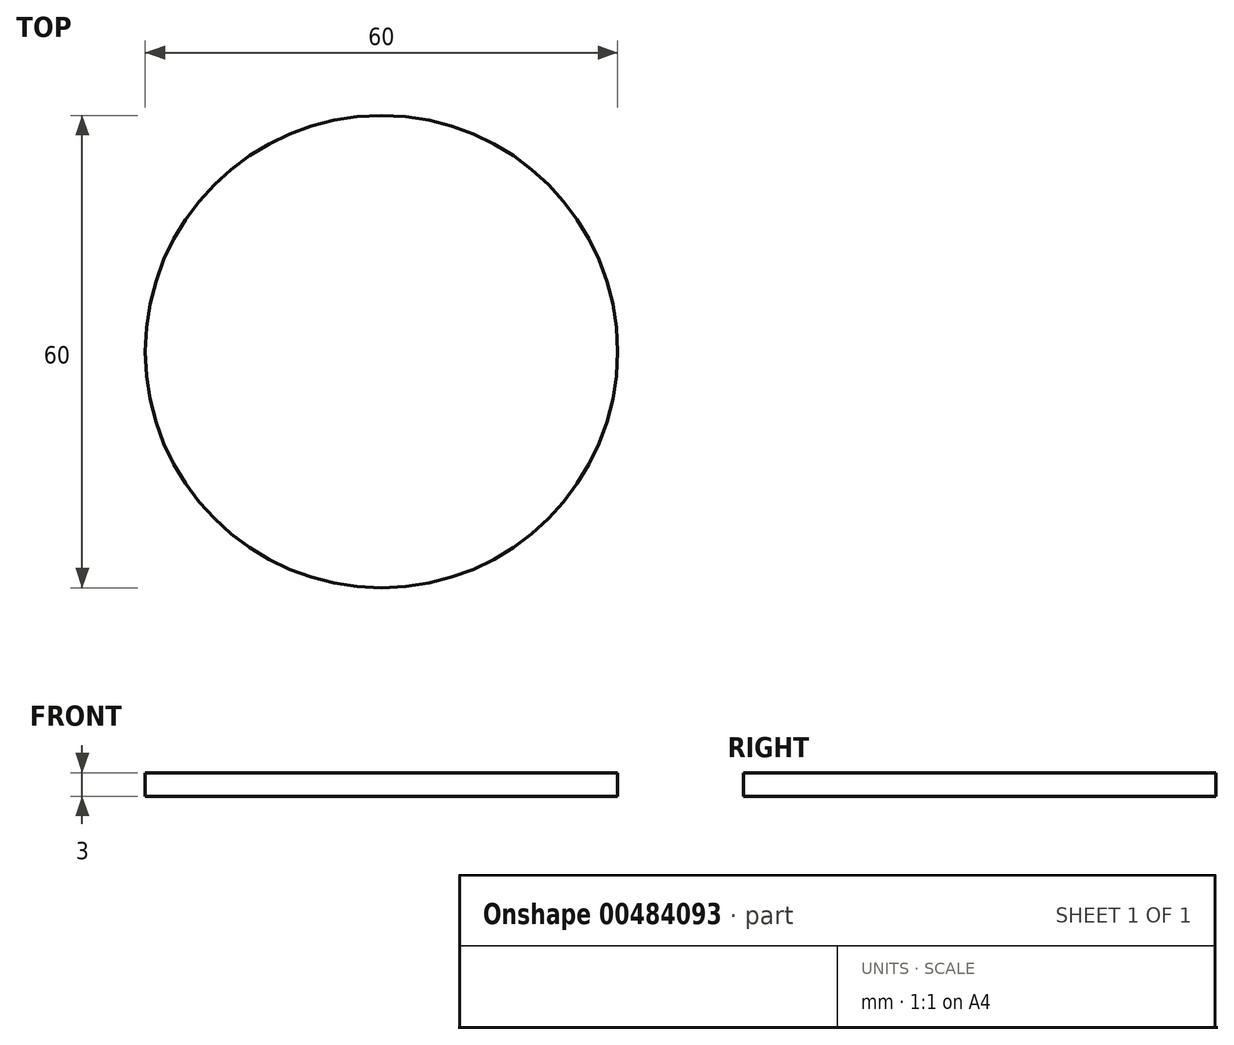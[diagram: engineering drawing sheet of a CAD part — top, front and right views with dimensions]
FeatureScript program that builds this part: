
annotation { "Feature Type Name" : "Feature", "Feature Type Description" : "" }
export const myFeature = defineFeature(function(context is Context, id is Id, definition is map)
    precondition{}
    {
        {
            var Q0;
            Q0=qCreatedBy(makeId("Top.planeOp"),FACE);
            var sketch = newSketch(context, id + "F0", { "sketchPlane" : qUnion([Q0])});
            skCircle(sketch, "E0", {"center": v(0, 0) * mm, "radius": 30 * mm});
            skSolve(sketch);
        }
        {
            var Q0;
            Q0=makeQuery(id+"F0.imprint","IMPRINT",FACE,{"disambiguationData":[TD([[makeQuery(id+"F0.imprint","IMPRINT",EDGE,{"derivedFrom":sQuery(id+"F0.wireOp",EDGE,"E0")}),1.0]])]});
            extrude(context, id + "F1", {"entities" : qUnion([Q0]), "depth" : 3 * mm});
        }
    });
